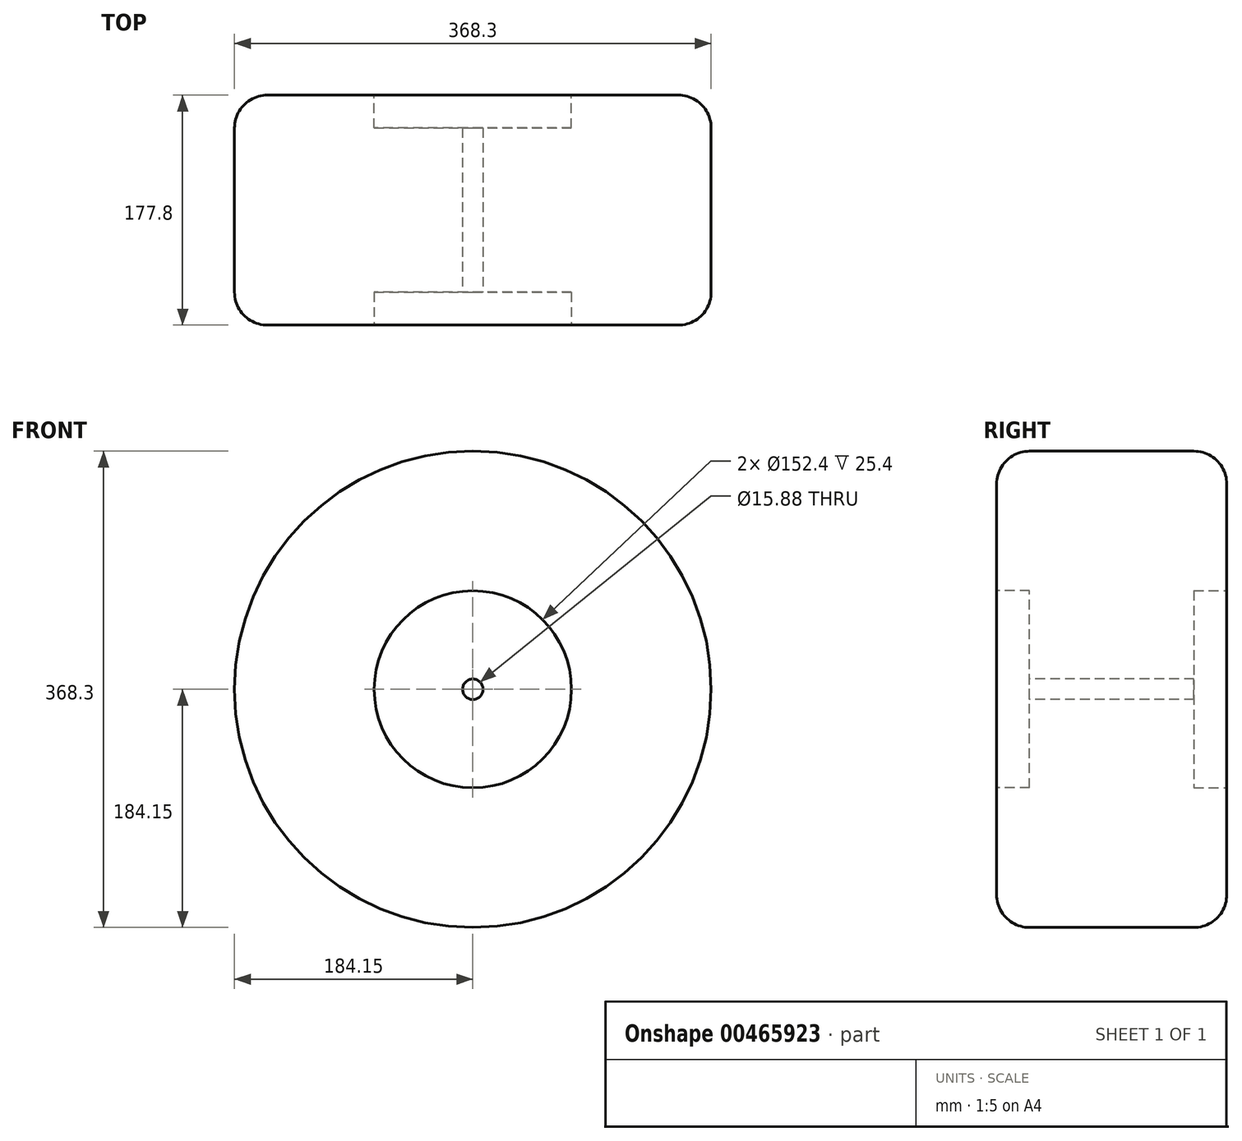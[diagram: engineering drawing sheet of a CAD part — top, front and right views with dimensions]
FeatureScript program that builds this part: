
annotation { "Feature Type Name" : "Feature", "Feature Type Description" : "" }
export const myFeature = defineFeature(function(context is Context, id is Id, definition is map)
    precondition{}
    {
        {
            var Q0;
            Q0=qCreatedBy(makeId("Front.planeOp"),FACE);
            var sketch = newSketch(context, id + "F0", { "sketchPlane" : qUnion([Q0])});
            skCircle(sketch, "E0", {"center": v(0, 0) * mm, "radius": 184.15 * mm});
            skSolve(sketch);
        }
        {
            var Q0;
            Q0=makeQuery(id+"F0.imprint","IMPRINT",FACE,{"disambiguationData":[TD([[makeQuery(id+"F0.imprint","IMPRINT",EDGE,{"derivedFrom":sQuery(id+"F0.wireOp",EDGE,"E0")}),1.0]])]});
            extrude(context, id + "F1", {"entities" : qUnion([Q0]), "endBound" : BoundingType.SYMMETRIC, "depth" : 177.8 * mm});
        }
        {
            var Q0;
            Q0=makeQuery(id+"F1.opExtrude","CAP_FACE",FACE,{"disambiguationData":[OSD([sQuery(id+"F0.wireOp",EDGE,"E0")])],"isStart":false});
            var sketch = newSketch(context, id + "F2", { "sketchPlane" : qUnion([Q0])});
            skCircle(sketch, "E1", {"center": v(0, 0) * mm, "radius": 76.2 * mm});
            skSolve(sketch);
        }
        {
            var Q0;
            Q0=makeQuery(id+"F2.imprint","IMPRINT",FACE,{"disambiguationData":[TD([[makeQuery(id+"F2.imprint","IMPRINT",EDGE,{"derivedFrom":sQuery(id+"F2.wireOp",EDGE,"E1")}),1.0]])]});
            extrude(context, id + "F3", {"entities" : qUnion([Q0]), "operationType" : NewBodyOperationType.REMOVE, "oppositeDirection" : true, "depth" : 25.4 * mm});
        }
        {
            var Q0;
            Q0=makeQuery(id+"F1.opExtrude","CAP_FACE",FACE,{"disambiguationData":[OSD([sQuery(id+"F0.wireOp",EDGE,"E0")])],"isStart":true});
            var sketch = newSketch(context, id + "F4", { "sketchPlane" : qUnion([Q0])});
            skCircle(sketch, "E2", {"center": v(0, 0) * mm, "radius": 76.2 * mm});
            skSolve(sketch);
        }
        {
            var Q0;
            Q0=makeQuery(id+"F4.imprint","IMPRINT",FACE,{"disambiguationData":[TD([[makeQuery(id+"F4.imprint","IMPRINT",EDGE,{"derivedFrom":sQuery(id+"F4.wireOp",EDGE,"E2")}),1.0]])]});
            extrude(context, id + "F5", {"entities" : qUnion([Q0]), "operationType" : NewBodyOperationType.REMOVE, "oppositeDirection" : true, "depth" : 25.4 * mm});
        }
        {
            var Q0;
            Q0=makeQuery(id+"F1.opExtrude","CAP_FACE",FACE,{"disambiguationData":[OSD([sQuery(id+"F0.wireOp",EDGE,"E0")])],"isStart":false});
            var sketch = newSketch(context, id + "F6", { "sketchPlane" : qUnion([Q0])});
            skCircle(sketch, "E3", {"center": v(0, 0) * mm, "radius": 12.7 * mm});
            skSolve(sketch);
        }
        {
            var Q0;
            Q0=makeQuery(id+"F6.imprint","IMPRINT",FACE,{"disambiguationData":[TD([[makeQuery(id+"F6.imprint","IMPRINT",EDGE,{"derivedFrom":sQuery(id+"F6.wireOp",EDGE,"E3")}),1.0]])]});
            extrude(context, id + "F7", {"entities" : qUnion([Q0]), "operationType" : NewBodyOperationType.REMOVE, "endBound" : BoundingType.SYMMETRIC, "depth" : 355.6 * mm});
        }
        {
            var Q0;
            Q0=makeQuery(id+"F1.opExtrude","CAP_EDGE",EDGE,{"disambiguationData":[OSD([sQuery(id+"F0.wireOp",EDGE,"E0")])],"isStart":true});
            var Q1;
            Q1=makeQuery(id+"F1.opExtrude","CAP_EDGE",EDGE,{"disambiguationData":[OSD([sQuery(id+"F0.wireOp",EDGE,"E0")])],"isStart":false});
            fillet(context, id + "F8", {"entities" : qUnion([Q0, Q1]), "radius" : 25.4 * mm, "tangentPropagation" : true, "allowEdgeOverflow" : false});
        }
        {
            var Q0;
            Q0=makeQuery(id+"F3.boolean.opBoolean","COPY",FACE,{"derivedFrom":makeQuery(id+"F3.opExtrude","CAP_FACE",FACE,{"disambiguationData":[OSD([sQuery(id+"F2.wireOp",EDGE,"E1")])],"isStart":false})});
            var sketch = newSketch(context, id + "F9", { "sketchPlane" : qUnion([Q0])});
            skCircle(sketch, "E4", {"center": v(0, 0) * mm, "radius": 7.94 * mm});
            skSolve(sketch);
        }
        {
            var Q0;
            Q0=makeQuery(id+"F9.imprint","IMPRINT",FACE,{"disambiguationData":[TD([[makeQuery(id+"F9.imprint","IMPRINT",EDGE,{"derivedFrom":sQuery(id+"F9.wireOp",EDGE,"E4")}),-1.0]])]});
            extrude(context, id + "F10", {"entities" : qUnion([Q0]), "operationType" : NewBodyOperationType.ADD, "depth" : -127 * mm});
        }
    });
